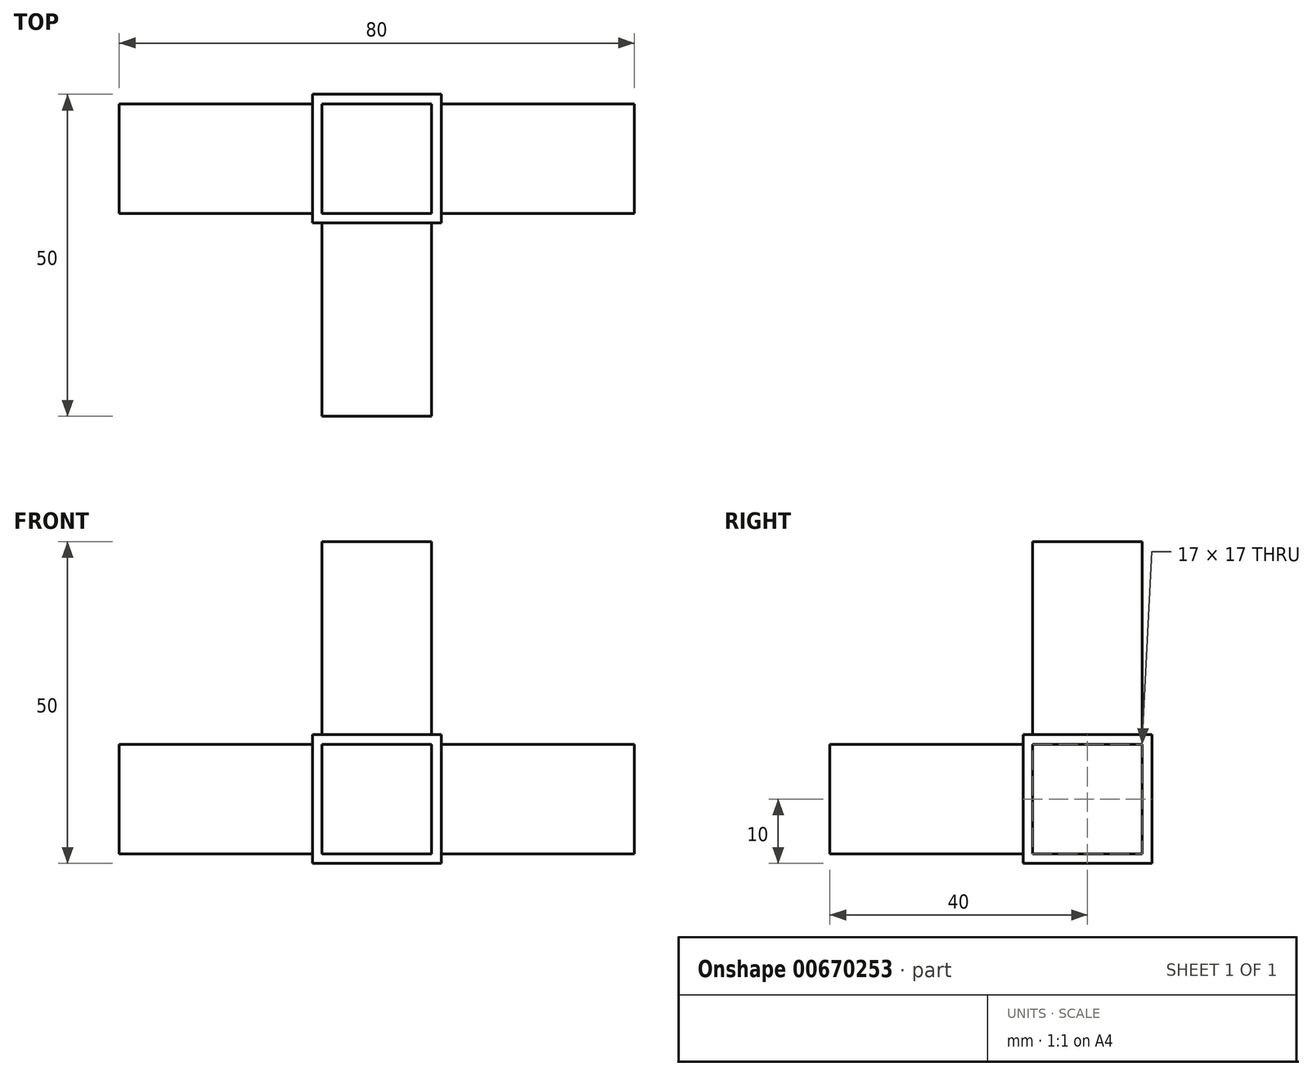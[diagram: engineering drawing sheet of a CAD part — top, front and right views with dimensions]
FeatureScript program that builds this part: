
annotation { "Feature Type Name" : "Feature", "Feature Type Description" : "" }
export const myFeature = defineFeature(function(context is Context, id is Id, definition is map)
    precondition{}
    {
        {
            var Q0;
            Q0=qCreatedBy(makeId("Front.planeOp"),FACE);
            var sketch = newSketch(context, id + "F0", { "sketchPlane" : qUnion([Q0])});
            skLineSegment(sketch, "E0.bottom", {"start": v(-10, -10) * mm, "end": v(10, -10) * mm});
            skLineSegment(sketch, "E0.top", {"start": v(-10, 10) * mm, "end": v(10, 10) * mm});
            skLineSegment(sketch, "E0.left", {"start": v(-10, -10) * mm, "end": v(-10, 10) * mm});
            skLineSegment(sketch, "E0.right", {"start": v(10, -10) * mm, "end": v(10, 10) * mm});
            skSolve(sketch);
        }
        {
            var Q0;
            Q0 = qSketchRegion(id + "F0", true);
            extrude(context, id + "F1", {"entities" : qUnion([Q0]), "depth" : 20 * mm, "offsetDistance" : 25 * mm});
        }
        {
            var Q0;
            Q0=makeQuery(id+"F1.opExtrude","SWEPT_BODY",BODY,{"disambiguationData":[OSD([sQuery(id+"F0.wireOp",EDGE,"E0.bottom"),sQuery(id+"F0.wireOp",EDGE,"E0.top"),sQuery(id+"F0.wireOp",EDGE,"E0.left"),sQuery(id+"F0.wireOp",EDGE,"E0.right")])]});
            var Q1;
            Q1=qCreatedBy(makeId("Front.planeOp"),FACE);
            transform(context, id + "F2", {"entities" : qUnion([Q0]), "transformType" : TransformType.TRANSLATION_DISTANCE, "transformDirection" : qUnion([Q1]), "distance" : 10 * mm, "oppositeDirection" : true, "makeCopy" : false});
        }
        {
            var Q0;
            Q0=makeQuery(id+"F1.opExtrude","CAP_FACE",FACE,{"disambiguationData":[OSD([sQuery(id+"F0.wireOp",EDGE,"E0.bottom"),sQuery(id+"F0.wireOp",EDGE,"E0.top"),sQuery(id+"F0.wireOp",EDGE,"E0.left"),sQuery(id+"F0.wireOp",EDGE,"E0.right")])],"isStart":false});
            var sketch = newSketch(context, id + "F3", { "sketchPlane" : qUnion([Q0])});
            skLineSegment(sketch, "E1.bottom", {"start": v(-8.5, 8.5) * mm, "end": v(8.5, 8.5) * mm});
            skLineSegment(sketch, "E1.top", {"start": v(-8.5, -8.5) * mm, "end": v(8.5, -8.5) * mm});
            skLineSegment(sketch, "E1.left", {"start": v(-8.5, 8.5) * mm, "end": v(-8.5, -8.5) * mm});
            skLineSegment(sketch, "E1.right", {"start": v(8.5, 8.5) * mm, "end": v(8.5, -8.5) * mm});
            skSolve(sketch);
        }
        {
            var Q0;
            Q0 = qSketchRegion(id + "F3", true);
            extrude(context, id + "F4", {"entities" : qUnion([Q0]), "operationType" : NewBodyOperationType.ADD, "depth" : 30 * mm, "offsetDistance" : 25 * mm});
        }
        {
            var Q0;
            Q0=makeQuery(id+"F1.opExtrude","SWEPT_FACE",FACE,{"disambiguationData":[OSD([sQuery(id+"F0.wireOp",EDGE,"E0.right")])]});
            var sketch = newSketch(context, id + "F5", { "sketchPlane" : qUnion([Q0])});
            skLineSegment(sketch, "E2.bottom", {"start": v(-8.5, 8.5) * mm, "end": v(8.5, 8.5) * mm});
            skLineSegment(sketch, "E2.top", {"start": v(-8.5, -8.5) * mm, "end": v(8.5, -8.5) * mm});
            skLineSegment(sketch, "E2.left", {"start": v(-8.5, 8.5) * mm, "end": v(-8.5, -8.5) * mm});
            skLineSegment(sketch, "E2.right", {"start": v(8.5, 8.5) * mm, "end": v(8.5, -8.5) * mm});
            skSolve(sketch);
        }
        {
            var Q0;
            Q0 = qSketchRegion(id + "F5", true);
            extrude(context, id + "F6", {"entities" : qUnion([Q0]), "operationType" : NewBodyOperationType.ADD, "depth" : 30 * mm, "offsetDistance" : 25 * mm});
        }
        {
            var Q0;
            Q0=makeQuery(id+"F1.opExtrude","SWEPT_FACE",FACE,{"disambiguationData":[OSD([sQuery(id+"F0.wireOp",EDGE,"E0.top")])]});
            var sketch = newSketch(context, id + "F7", { "sketchPlane" : qUnion([Q0])});
            skLineSegment(sketch, "E3.bottom", {"start": v(-8.5, 8.5) * mm, "end": v(8.5, 8.5) * mm});
            skLineSegment(sketch, "E3.top", {"start": v(-8.5, -8.5) * mm, "end": v(8.5, -8.5) * mm});
            skLineSegment(sketch, "E3.left", {"start": v(-8.5, 8.5) * mm, "end": v(-8.5, -8.5) * mm});
            skLineSegment(sketch, "E3.right", {"start": v(8.5, 8.5) * mm, "end": v(8.5, -8.5) * mm});
            skSolve(sketch);
        }
        {
            var Q0;
            Q0 = qSketchRegion(id + "F7", true);
            extrude(context, id + "F8", {"entities" : qUnion([Q0]), "operationType" : NewBodyOperationType.ADD, "depth" : 30 * mm, "offsetDistance" : 25 * mm});
        }
        {
            var Q0;
            Q0=makeQuery(id+"F1.opExtrude","SWEPT_FACE",FACE,{"disambiguationData":[OSD([sQuery(id+"F0.wireOp",EDGE,"E0.left")])]});
            var sketch = newSketch(context, id + "F9", { "sketchPlane" : qUnion([Q0])});
            skLineSegment(sketch, "E4.bottom", {"start": v(-8.5, 8.5) * mm, "end": v(8.5, 8.5) * mm});
            skLineSegment(sketch, "E4.top", {"start": v(-8.5, -8.5) * mm, "end": v(8.5, -8.5) * mm});
            skLineSegment(sketch, "E4.left", {"start": v(-8.5, 8.5) * mm, "end": v(-8.5, -8.5) * mm});
            skLineSegment(sketch, "E4.right", {"start": v(8.5, 8.5) * mm, "end": v(8.5, -8.5) * mm});
            skSolve(sketch);
        }
        {
            var Q0;
            Q0 = qSketchRegion(id + "F9", true);
            extrude(context, id + "F10", {"entities" : qUnion([Q0]), "operationType" : NewBodyOperationType.ADD, "depth" : 30 * mm, "offsetDistance" : 25 * mm});
        }
    });
